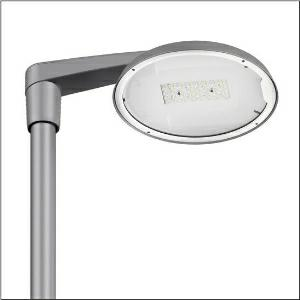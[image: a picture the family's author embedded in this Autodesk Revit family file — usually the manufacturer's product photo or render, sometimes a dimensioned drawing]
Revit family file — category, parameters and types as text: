
# Revit family: dl_r__50_iq_mini___st0_5a_5xa248b31f08je_331a
name_source: partatom
category: Lighting Fixtures
units: mm (PartAtom-declared; Revit-internal decimal feet)

## family parameters
Cut with Voids When Loaded = No
Host = Face
Light Source = No
Part Type = Normal
Room Calculation Point = No
Round Connector Dimension = Use Diameter
Shared = No

## types (1)
- --- (1 x LED, 10300 lm, 66 W, 3000K)
    Apparent Load = 66 VA
    CIE Flux Codes = 43 76 97 100 100
    Color Rendering = 70
    Color Temperature = 3000K
    Default Elevation = 1800 mm
    Description = DL® 50 iQ mini, mast luminaire, primary light control with lens, of PMMA, primary optical cover: cover, of toughened safety glass, transparent, light distribution: ST0.5a, light emission: direct distribution, primary light characteristic: asymmetric, installation type: side-entry, post-top, LED, High Power LED, rated luminous flux: 10.300lm, luminous efficacy: 156lm/W, light colour: 730, colour temperature: 3000K, control gear: iQ Street-Remote, control: optimised constant luminous flux control (CLO 2.0), Desk-Remote (wireless, voltage-free reading and setting of iQ features in the workshop via application-optimized NFC function/RFID function), Light-Fading, Smart-Wire, Night-Set, Lumen-Switch, Temp-Guard, Auto-Match, Street-Remote, mains connection: 230..240V, AC, 50/60Hz, connection cable pre-assembled, cable length: 8,5m, start of lifetime: 66W, end of service life: 69W, reduction: 30W, luminaire housing, of diecast aluminium, powder-coated, Siteco® metallic grey (DB 702S), inclination adjustable: 0°, 5°, 10° (post-top) | 0°, -5°, -10°, -15° (side-entry), please order mast post-top element or mast side-entry element separately, diameter: 500mm, height: 115mm, post-top: for spigot size d x l = 76 x 100mm; with reducer (optional accessory) 60 x 100mm | side-entry: for spigot size d x l = 60 x 100mm; with reducer (optional accessory) 42 x 100mm, mounting height: 4..6m, protection rating (complete): IP66, insulation class (complete): insulation class II (safety insulation), certification: CE, ENEC, ENEC+, VDE, impact resistance: IK08, permissible operating ambient temperature for outdoor applications: -25..+40°C, standard-compliant lighting for roads and squares, packaging unit: 1 piece

Light Distribution: ST0.5a
    Height = 115 mm
    Lamp = 1 x LED
    Lamp Light Flux = 10300 lm
    Lamp Power = 66 W
    Lamp count = 1
    Length = 500 mm
    Luminous efficacy = 156 lm/W
    Manufacturer = Siteco
    ModVariant = No
    Model = 5XA248B31F08JE
    Number of Poles = 1
    OnlyDefault = Yes
    Power Factor = 1
    Product Name = DL® 50 iQ mini | ST0.5a
    Product group = mast luminaire | pylon top
    ProductGroupID = 6100
    Protection Class = Protection class II
    Protection Degree = IP 66
    RLX_Detail_Level = 1
    RLX_Emergency_Light_Flux = 0 lm
    RLX_Emergency_Type = 0
    RLX_Emergency_Type_DB = No
    RlxData = <blob elided: 126757 chars, md5=2269ee52>
    Socket = socket
    Standby Power = 0 W
    System Light Flux = 10300 lm
    System Power = 66 W
    Type Comments = factory setting: luminous flux: 100 % | dim-lin: 254 | 693 mA
    Type Image = l_1251794.jpg
    URL = http://relux.com
    VarID = @adj_164399
    Voltage = 0 V
    Weight = 0.00 kg
    Width = 0 mm  [stored 0 ft]

note: [stored X ft] marks values corroborated as IEEE doubles in the binary element streams (Revit-internal decimal feet)

## geometry (parser evidence)
native form markers: Blend x4, Sweep x12
no freeform markers — native parametric forms only
